# Revit family: Hager-UNIVERS-Surface_mounted-IP44-With_Cover-With_DIN-NoHosted-SE-en
name_source: partatom
category: Electrical Equipment
units: mm (PartAtom-declared; Revit-internal decimal feet)

## family parameters
Always vertical = Yes
Cut with Voids When Loaded = No
Maintain Annotation Orientation = No
Panel Configuration = Two Columns, Circuits Across
Part Type = Panelboard
Room Calculation Point = No
Round Connector Dimension = Use Diameter
Shared = No
Work Plane-Based = Yes

## types (20) — shared parameters
Code hager = ADD-EC000214_EU
Default Elevation = 1200 mm
EF000007 - Colour = White
EF000024 - UV resistant = No
EF000049 - Depth = 165 mm
EF000116 - RAL-number = 9010
EF000118 - With mounting plate = No
EF000218 - Built-in depth = 161 mm  [stored 0.528215 ft]
EF001062 - EMC-version = No
EF001088 - Extension possible = Yes
EF001134 - DIN-rail = Yes
EF004462 - Type of closure = Other
EF005474 - Degree of protection (IP) = IP44
EF006244 - Transparent cover/door = No
EF006306 - With lock = No
EF009212 - Cover model = With notch
EF015776 - Earthing terminal block = Yes
EF015777 - Neutral terminal block = Yes
EF015941 - Signal passing door = No
ETIM class code = EC000214
ETIM class name = Small distribution board
HG000002-With door or cover = Yes
HG000003-Range = UNIVERS
HG000005-Thickness = 2 mm  [stored 0.00656168 ft]
HG000006-Flush mounted = No
HG000011-Empty rows from bottom = No
HG000012-Door swing angle = 90.00°
HG000013-Door on the left = No
HG000014-Door on the right = Yes
HG000015-Clearance visibility = Yes
HG000016-Door 3D visibility = Yes
HG000017-Distance between poles = 18 mm  [stored 0.0590551 ft]
HG000060-RAL-number = 9010
HG000099-Onfly Template ID = 507532
Manufacturer = Hager
Name BIM&CO = Electricity
Name hager = ADD_Enclosures_EC000214
Reference = Template-Enclosure_EU-EC000214
Uniformat = Low Tension Service & Dist.
Uniformat code = D501001
zero-valued in all types: EF001131 - Inner depth, HG000007-Number of empty columns, HG000008-Number of empty rows

## per-type parameters (varying)
| type | BC_METADATA | EF000003 - Mounting method | EF000008 - Width | EF000040 - Height | EF000266 - Number of rows | EF000332 - Built-in height | EF000846 - Built-in width | EF002950 - Width in number of modular spacings | HG000001-Number of columns | HG000004-Manufacturer reference | HG000009-Double swing door | HG000010-Asymmetric doors | HGEF000266-Number of rows | HGEF002950-Width in number of modular spacings |
| UNIVERS-Surface_mounted_W300_H500_D165_12_Modular_Spacing-FWB31S | {"ObjectGuid":"37693fbf-5dcc-4b09-9ade-bc6b5046593d","ModelGuid":"bf280334-d779-4d5b-88e6-d170924b41af","VariantGuid":"91413721-646e-4707-8b69-972fa6666271","Revision":"#3","VariantName":"UNIVERS-Surface_mounted_W300_H500_D165_12_Modular_Spacing-FWB31S"} | Surface mounted | 300 mm | 500 mm  [stored 1.64042 ft] | 3 | 500 mm  [stored 1.64042 ft] | 300 mm | 12 | 1 | FWB31S | No | No | 3 | 12 |
| UNIVERS-Surface_mounted_W550_H500_D165_24_Modular_Spacing-FWB32S | {"ObjectGuid":"37693fbf-5dcc-4b09-9ade-bc6b5046593d","ModelGuid":"bf280334-d779-4d5b-88e6-d170924b41af","VariantGuid":"bf76f1c8-e976-4b73-bce6-bf95bd4beabd","Revision":"#3","VariantName":"UNIVERS-Surface_mounted_W550_H500_D165_24_Modular_Spacing-FWB32S"} | Surface mounted | 550 mm | 500 mm  [stored 1.64042 ft] | 3 | 500 mm  [stored 1.64042 ft] | 550 mm | 24 | 2 | FWB32S | No | No | 3 | 24 |
| UNIVERS-Surface_mounted_W800_H500_D165_36_Modular_Spacing-FWB33S | {"ObjectGuid":"37693fbf-5dcc-4b09-9ade-bc6b5046593d","ModelGuid":"bf280334-d779-4d5b-88e6-d170924b41af","VariantGuid":"66f19b9a-3ee9-48e2-a394-df79ccb43efe","Revision":"#3","VariantName":"UNIVERS-Surface_mounted_W800_H500_D165_36_Modular_Spacing-FWB33S"} | Surface mounted | 800 mm  [stored 2.62467 ft] | 500 mm  [stored 1.64042 ft] | 3 | 500 mm  [stored 1.64042 ft] | 800 mm  [stored 2.62467 ft] | 36 | 3 | FWB33S | Yes | Yes | 3 | 36 |
| UNIVERS-Surface_mounted_W1050_H500_D165_48_Modular_Spacing-FWB34S | {"ObjectGuid":"37693fbf-5dcc-4b09-9ade-bc6b5046593d","ModelGuid":"bf280334-d779-4d5b-88e6-d170924b41af","VariantGuid":"0777e640-4e84-4bcd-8333-3e39a2f9670e","Revision":"#3","VariantName":"UNIVERS-Surface_mounted_W1050_H500_D165_48_Modular_Spacing-FWB34S"} | Surface mounted | 1050 mm  [stored 3.44488 ft] | 500 mm  [stored 1.64042 ft] | 3 | 500 mm  [stored 1.64042 ft] | 1050 mm  [stored 3.44488 ft] | 48 | 4 | FWB34S | Yes | No | 3 | 48 |
| UNIVERS-Surface_mounted_W300_H650_D165_12_Modular_Spacing-FWB41S | {"ObjectGuid":"37693fbf-5dcc-4b09-9ade-bc6b5046593d","ModelGuid":"bf280334-d779-4d5b-88e6-d170924b41af","VariantGuid":"7f72389e-0a7b-4619-9953-d179f0ba8bf1","Revision":"#3","VariantName":"UNIVERS-Surface_mounted_W300_H650_D165_12_Modular_Spacing-FWB41S"} | Surface mounted | 300 mm | 650 mm  [stored 2.13255 ft] | 4 | 650 mm  [stored 2.13255 ft] | 300 mm | 12 | 1 | FWB41S | No | No | 4 | 12 |
| UNIVERS-Surface_mounted_W550_H650_D165_24_Modular_Spacing-FWB42S | {"ObjectGuid":"37693fbf-5dcc-4b09-9ade-bc6b5046593d","ModelGuid":"bf280334-d779-4d5b-88e6-d170924b41af","VariantGuid":"51a01e33-784f-4c04-a816-8775363e5a77","Revision":"#3","VariantName":"UNIVERS-Surface_mounted_W550_H650_D165_24_Modular_Spacing-FWB42S"} | Surface mounted/recessed mounted | 550 mm | 650 mm  [stored 2.13255 ft] | 4 | 650 mm  [stored 2.13255 ft] | 550 mm | 24 | 2 | FWB42S | No | No | 4 | 24 |
| UNIVERS-Surface_mounted_W800_H650_D165_36_Modular_Spacing-FWB43S | {"ObjectGuid":"37693fbf-5dcc-4b09-9ade-bc6b5046593d","ModelGuid":"bf280334-d779-4d5b-88e6-d170924b41af","VariantGuid":"41b38856-586e-4d1f-84ce-b8157199a9ee","Revision":"#3","VariantName":"UNIVERS-Surface_mounted_W800_H650_D165_36_Modular_Spacing-FWB43S"} | Surface mounted | 800 mm  [stored 2.62467 ft] | 650 mm  [stored 2.13255 ft] | 4 | 650 mm  [stored 2.13255 ft] | 800 mm  [stored 2.62467 ft] | 36 | 3 | FWB43S | Yes | Yes | 4 | 36 |
| UNIVERS-Surface_mounted_W1050_H650_D165_48_Modular_Spacing-FWB44S | {"ObjectGuid":"37693fbf-5dcc-4b09-9ade-bc6b5046593d","ModelGuid":"bf280334-d779-4d5b-88e6-d170924b41af","VariantGuid":"d22ded24-c5b1-4f8b-8c9c-344c1e79098e","Revision":"#3","VariantName":"UNIVERS-Surface_mounted_W1050_H650_D165_48_Modular_Spacing-FWB44S"} | Surface mounted | 1050 mm  [stored 3.44488 ft] | 650 mm  [stored 2.13255 ft] | 4 | 650 mm  [stored 2.13255 ft] | 1050 mm  [stored 3.44488 ft] | 48 | 4 | FWB44S | Yes | No | 4 | 48 |
| UNIVERS-Surface_mounted_W300_H800_D165_12_Modular_Spacing-FWB51S | {"ObjectGuid":"37693fbf-5dcc-4b09-9ade-bc6b5046593d","ModelGuid":"bf280334-d779-4d5b-88e6-d170924b41af","VariantGuid":"faa41bcb-b9a6-46bf-b7f2-907395c7259a","Revision":"#3","VariantName":"UNIVERS-Surface_mounted_W300_H800_D165_12_Modular_Spacing-FWB51S"} | Surface mounted | 300 mm | 800 mm  [stored 2.62467 ft] | 5 | 800 mm  [stored 2.62467 ft] | 300 mm | 12 | 1 | FWB51S | No | No | 5 | 12 |
| UNIVERS-Surface_mounted_W550_H800_D165_24_Modular_Spacing-FWB52S | {"ObjectGuid":"37693fbf-5dcc-4b09-9ade-bc6b5046593d","ModelGuid":"bf280334-d779-4d5b-88e6-d170924b41af","VariantGuid":"a6fcc2ce-a7f2-451b-9d7f-563beddb556e","Revision":"#3","VariantName":"UNIVERS-Surface_mounted_W550_H800_D165_24_Modular_Spacing-FWB52S"} | Surface mounted | 550 mm | 800 mm  [stored 2.62467 ft] | 5 | 800 mm  [stored 2.62467 ft] | 550 mm | 24 | 2 | FWB52S | No | No | 5 | 24 |
| UNIVERS-Surface_mounted_W800_H800_D165_36_Modular_Spacing-FWB53S | {"ObjectGuid":"37693fbf-5dcc-4b09-9ade-bc6b5046593d","ModelGuid":"bf280334-d779-4d5b-88e6-d170924b41af","VariantGuid":"f616ce28-90a9-4aba-81f5-a068a1456a0c","Revision":"#3","VariantName":"UNIVERS-Surface_mounted_W800_H800_D165_36_Modular_Spacing-FWB53S"} | Surface mounted | 800 mm  [stored 2.62467 ft] | 800 mm  [stored 2.62467 ft] | 5 | 800 mm  [stored 2.62467 ft] | 800 mm  [stored 2.62467 ft] | 36 | 3 | FWB53S | Yes | Yes | 5 | 36 |
| UNIVERS-Surface_mounted_W1050_H800_D165_48_Modular_Spacing-FWB54S | {"ObjectGuid":"37693fbf-5dcc-4b09-9ade-bc6b5046593d","ModelGuid":"bf280334-d779-4d5b-88e6-d170924b41af","VariantGuid":"db708c5d-143e-421c-b305-c141cd963cc2","Revision":"#3","VariantName":"UNIVERS-Surface_mounted_W1050_H800_D165_48_Modular_Spacing-FWB54S"} | Surface mounted | 1050 mm  [stored 3.44488 ft] | 800 mm  [stored 2.62467 ft] | 5 | 800 mm  [stored 2.62467 ft] | 1050 mm  [stored 3.44488 ft] | 48 | 4 | FWB54S | Yes | No | 5 | 48 |
| UNIVERS-Surface_mounted_W300_H950_D165_12_Modular_Spacing-FWB61S | {"ObjectGuid":"37693fbf-5dcc-4b09-9ade-bc6b5046593d","ModelGuid":"bf280334-d779-4d5b-88e6-d170924b41af","VariantGuid":"4a42fc14-2224-46c5-a4f5-410e0409a254","Revision":"#3","VariantName":"UNIVERS-Surface_mounted_W300_H950_D165_12_Modular_Spacing-FWB61S"} | Surface mounted | 300 mm | 950 mm  [stored 3.1168 ft] | 6 | 950 mm  [stored 3.1168 ft] | 300 mm | 12 | 1 | FWB61S | No | No | 6 | 12 |
| UNIVERS-Surface_mounted_W550_H950_D165_24_Modular_Spacing-FWB62S | {"ObjectGuid":"37693fbf-5dcc-4b09-9ade-bc6b5046593d","ModelGuid":"bf280334-d779-4d5b-88e6-d170924b41af","VariantGuid":"c650b6da-32f9-4a00-93b6-b362cf9521cb","Revision":"#3","VariantName":"UNIVERS-Surface_mounted_W550_H950_D165_24_Modular_Spacing-FWB62S"} | Surface mounted | 550 mm | 950 mm  [stored 3.1168 ft] | 6 | 950 mm  [stored 3.1168 ft] | 550 mm | 24 | 2 | FWB62S | No | No | 6 | 24 |
| UNIVERS-Surface_mounted_W800_H950_D165_36_Modular_Spacing-FWB63S | {"ObjectGuid":"37693fbf-5dcc-4b09-9ade-bc6b5046593d","ModelGuid":"bf280334-d779-4d5b-88e6-d170924b41af","VariantGuid":"5224079d-430f-48af-83fd-30711c7faeff","Revision":"#3","VariantName":"UNIVERS-Surface_mounted_W800_H950_D165_36_Modular_Spacing-FWB63S"} | Surface mounted | 800 mm  [stored 2.62467 ft] | 950 mm  [stored 3.1168 ft] | 6 | 950 mm  [stored 3.1168 ft] | 800 mm  [stored 2.62467 ft] | 36 | 3 | FWB63S | Yes | Yes | 6 | 36 |
| UNIVERS-Surface_mounted_W1050_H950_D165_48_Modular_Spacing-FWB64S | {"ObjectGuid":"37693fbf-5dcc-4b09-9ade-bc6b5046593d","ModelGuid":"bf280334-d779-4d5b-88e6-d170924b41af","VariantGuid":"57943910-8cec-4a90-996e-f81ec435d342","Revision":"#3","VariantName":"UNIVERS-Surface_mounted_W1050_H950_D165_48_Modular_Spacing-FWB64S"} | Surface mounted | 1050 mm  [stored 3.44488 ft] | 950 mm  [stored 3.1168 ft] | 6 | 950 mm  [stored 3.1168 ft] | 1050 mm  [stored 3.44488 ft] | 48 | 4 | FWB64S | Yes | No | 6 | 48 |
| UNIVERS-Surface_mounted_W300_H1100_D165_12_Modular_Spacing-FWB71S | {"ObjectGuid":"37693fbf-5dcc-4b09-9ade-bc6b5046593d","ModelGuid":"bf280334-d779-4d5b-88e6-d170924b41af","VariantGuid":"60ab50e9-be69-490f-8484-16eb568df245","Revision":"#3","VariantName":"UNIVERS-Surface_mounted_W300_H1100_D165_12_Modular_Spacing-FWB71S"} | Surface mounted | 300 mm | 1100 mm | 7 | 1100 mm | 300 mm | 12 | 1 | FWB71S | No | No | 7 | 12 |
| UNIVERS-Surface_mounted_W550_H1100_D165_24_Modular_Spacing-FWB72S | {"ObjectGuid":"37693fbf-5dcc-4b09-9ade-bc6b5046593d","ModelGuid":"bf280334-d779-4d5b-88e6-d170924b41af","VariantGuid":"dd2c687d-831e-4edc-affe-a06321410f05","Revision":"#3","VariantName":"UNIVERS-Surface_mounted_W550_H1100_D165_24_Modular_Spacing-FWB72S"} | Surface mounted/recessed mounted | 550 mm | 1100 mm | 7 | 1100 mm | 550 mm | 24 | 2 | FWB72S | No | No | 7 | 24 |
| UNIVERS-Surface_mounted_W800_H1100_D165_36_Modular_Spacing-FWB73S | {"ObjectGuid":"37693fbf-5dcc-4b09-9ade-bc6b5046593d","ModelGuid":"bf280334-d779-4d5b-88e6-d170924b41af","VariantGuid":"d45ebbc0-0caf-4b73-94f8-b6a7925d409c","Revision":"#3","VariantName":"UNIVERS-Surface_mounted_W800_H1100_D165_36_Modular_Spacing-FWB73S"} | Surface mounted/recessed mounted | 800 mm  [stored 2.62467 ft] | 1100 mm | 7 | 1100 mm | 800 mm  [stored 2.62467 ft] | 36 | 3 | FWB73S | Yes | Yes | 7 | 36 |
| UNIVERS-Surface_mounted_W1050_H1100_D165_48_Modular_Spacing-FWB74S | {"ObjectGuid":"37693fbf-5dcc-4b09-9ade-bc6b5046593d","ModelGuid":"bf280334-d779-4d5b-88e6-d170924b41af","VariantGuid":"51d3d3b9-9e61-4b51-83c9-43aa02cd38c4","Revision":"#3","VariantName":"UNIVERS-Surface_mounted_W1050_H1100_D165_48_Modular_Spacing-FWB74S"} | Surface mounted/recessed mounted | 1050 mm  [stored 3.44488 ft] | 1100 mm | 7 | 1100 mm | 1050 mm  [stored 3.44488 ft] | 48 | 4 | FWB74S | Yes | No | 7 | 48 |

note: [stored X ft] marks values corroborated as IEEE doubles in the binary element streams (Revit-internal decimal feet)

## geometry (parser evidence)
native form markers: Sweep x14
no freeform markers — native parametric forms only
